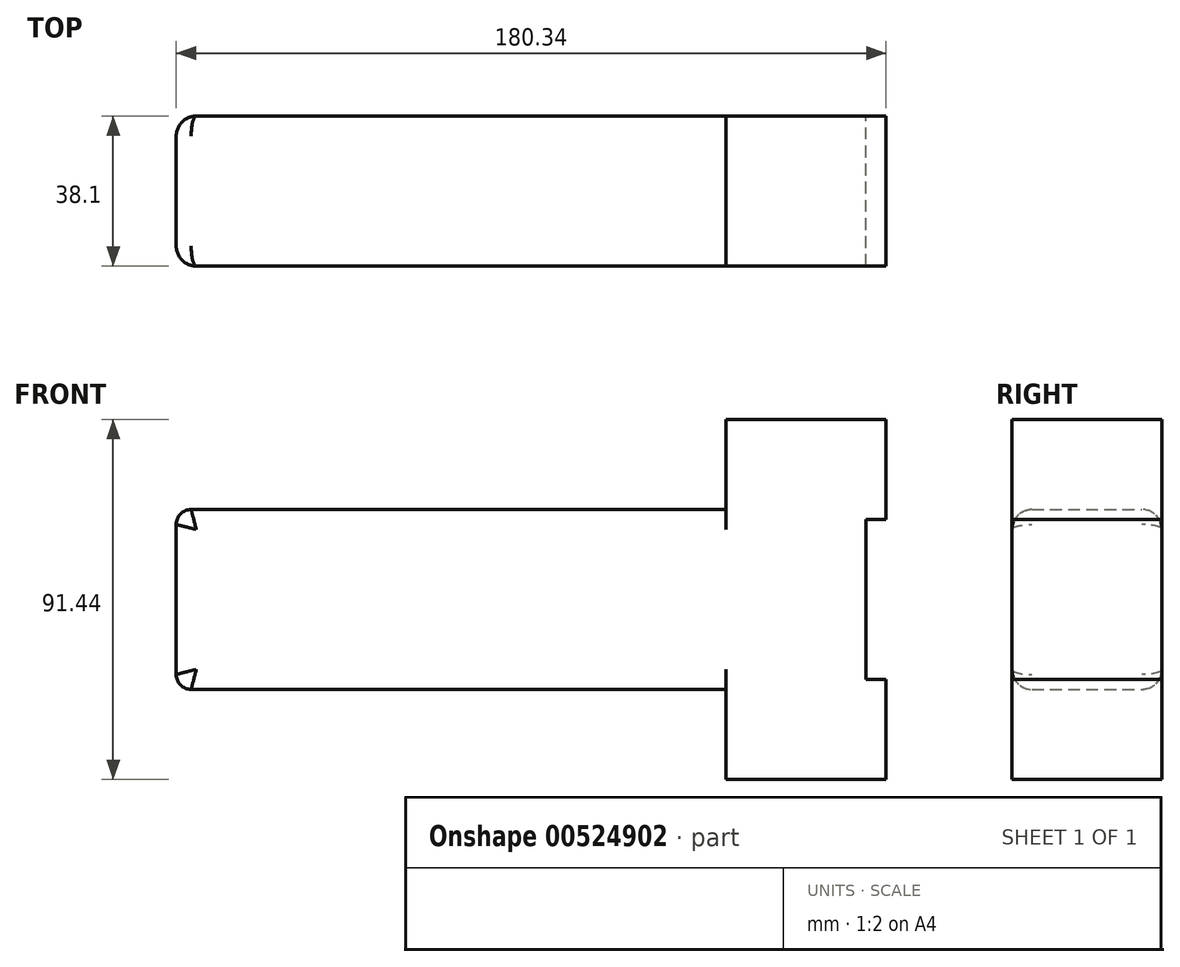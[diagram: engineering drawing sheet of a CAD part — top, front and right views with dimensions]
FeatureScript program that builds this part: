
annotation { "Feature Type Name" : "Feature", "Feature Type Description" : "" }
export const myFeature = defineFeature(function(context is Context, id is Id, definition is map)
    precondition{}
    {
        {
            var Q0;
            Q0=qCreatedBy(makeId("Front.planeOp"),FACE);
            var sketch = newSketch(context, id + "F0", { "sketchPlane" : qUnion([Q0])});
            skLineSegment(sketch, "E0.bottom", {"start": v(69.85, -22.86) * mm, "end": v(-66.04, -22.86) * mm});
            skLineSegment(sketch, "E0.top", {"start": v(69.85, 22.86) * mm, "end": v(-66.04, 22.86) * mm});
            skLineSegment(sketch, "E0.left", {"start": v(69.85, -22.86) * mm, "end": v(69.85, 22.86) * mm});
            skLineSegment(sketch, "E0.right", {"start": v(-69.85, -19.05) * mm, "end": v(-69.85, 19.05) * mm});
            skPoint(sketch, "E0.middle", {"position": v(0, 0) * mm});
            skLineSegment(sketch, "E1.bottom", {"start": v(110.5, -45.72) * mm, "end": v(69.85, -45.72) * mm});
            skLineSegment(sketch, "E1.top", {"start": v(110.5, 45.72) * mm, "end": v(69.85, 45.72) * mm});
            skLineSegment(sketch, "E1.left", {"start": v(110.5, -45.72) * mm, "end": v(110.5, -20.32) * mm});
            skLineSegment(sketch, "E1.right", {"start": v(69.85, -45.72) * mm, "end": v(69.85, 45.72) * mm});
            skPoint(sketch, "E1.middle", {"position": v(90.17, 0) * mm});
            skPoint(sketch, "E2.visualSharp", {"position": v(-69.85, 22.86) * mm});
            skArc(sketch, "E2.filletArc", {"start": v(-66.04, 22.86) * mm, "mid": v(-68.73, 21.74) * mm, "end": v(-69.85, 19.05) * mm});
            skPoint(sketch, "E3.visualSharp", {"position": v(-69.85, -22.86) * mm});
            skArc(sketch, "E3.filletArc", {"start": v(-69.85, -19.05) * mm, "mid": v(-68.73, -21.74) * mm, "end": v(-66.04, -22.86) * mm});
            skLineSegment(sketch, "E4", {"start": v(-69.85, -19.05) * mm, "end": v(31.75, -19.05) * mm});
            skLineSegment(sketch, "E5", {"start": v(-69.85, 19.05) * mm, "end": v(31.75, 19.05) * mm});
            skLineSegment(sketch, "E6", {"start": v(31.75, -22.86) * mm, "end": v(31.75, 22.86) * mm});
            skPoint(sketch, "E7", {"position": v(47, -22.86) * mm});
            skArc(sketch, "E8", {"start": v(31.75, -19.05) * mm, "mid": v(39.6, -20.02) * mm, "end": v(47, -22.86) * mm});
            skPoint(sketch, "E9", {"position": v(47, 22.86) * mm});
            skArc(sketch, "E10", {"start": v(31.75, 19.05) * mm, "mid": v(39.6, 20.02) * mm, "end": v(46.99, 22.86) * mm});
            skLineSegment(sketch, "E11.bottom", {"start": v(110.5, 20.32) * mm, "end": v(105.41, 20.32) * mm});
            skLineSegment(sketch, "E11.top", {"start": v(110.5, -20.32) * mm, "end": v(105.41, -20.32) * mm});
            skLineSegment(sketch, "E11.right", {"start": v(105.41, 20.32) * mm, "end": v(105.41, -20.32) * mm});
            skPoint(sketch, "E11.middle", {"position": v(110.5, 0) * mm});
            skLineSegment(sketch, "E12.trimOffspring", {"start": v(110.5, 20.32) * mm, "end": v(110.5, 45.72) * mm});
            skSolve(sketch);
        }
        {
            var Q0;
            {var subQ5=sQuery(id+"F0.wireOp",EDGE,"E8");Q0=makeQuery(id+"F0.imprint","IMPRINT",FACE,{"disambiguationData":[TD([[makeQuery(id+"F0.imprint","IMPRINT",EDGE,{"derivedFrom":subQ5}),1.0]])]});}
            var Q1;
            Q1=makeQuery(id+"F0.imprint","IMPRINT",FACE,{"disambiguationData":[TD([[makeQuery(id+"F0.imprint","IMPRINT",EDGE,{"derivedFrom":sQuery(id+"F0.wireOp",EDGE,"E0.right")}),-1.0]])]});
            var Q2;
            {var subQ0=sQuery(id+"F0.wireOp",EDGE,"E2.filletArc");Q2=makeQuery(id+"F0.imprint","IMPRINT",FACE,{"disambiguationData":[TD([[makeQuery(id+"F0.imprint","IMPRINT",EDGE,{"derivedFrom":subQ0}),1.0]])]});}
            var Q3;
            {var subQ3=sQuery(id+"F0.wireOp",EDGE,"E10");Q3=makeQuery(id+"F0.imprint","IMPRINT",FACE,{"disambiguationData":[TD([[makeQuery(id+"F0.imprint","IMPRINT",EDGE,{"derivedFrom":subQ3}),1.0]])]});}
            var Q4;
            {var subQ0=sQuery(id+"F0.wireOp",EDGE,"E3.filletArc");Q4=makeQuery(id+"F0.imprint","IMPRINT",FACE,{"disambiguationData":[TD([[makeQuery(id+"F0.imprint","IMPRINT",EDGE,{"derivedFrom":subQ0}),1.0]])]});}
            var Q5;
            {var subQ3=sQuery(id+"F0.wireOp",EDGE,"E8");Q5=makeQuery(id+"F0.imprint","IMPRINT",FACE,{"disambiguationData":[TD([[makeQuery(id+"F0.imprint","IMPRINT",EDGE,{"derivedFrom":subQ3}),-1.0]])]});}
            var Q6;
            {var subQ2=sQuery(id+"F0.wireOp",EDGE,"E1.bottom");Q6=makeQuery(id+"F0.imprint","IMPRINT",FACE,{"disambiguationData":[TD([[makeQuery(id+"F0.imprint","IMPRINT",EDGE,{"derivedFrom":subQ2}),-1.0]])]});}
            extrude(context, id + "F1", {"entities" : qUnion([Q0, Q1, Q2, Q3, Q4, Q5, Q6]), "depth" : 38.1 * mm, "offsetDistance" : 25.4 * mm});
        }
        {
            var Q0;
            Q0=makeQuery(id+"F1.opExtrude","CAP_EDGE",EDGE,{"disambiguationData":[OSD([sQuery(id+"F0.wireOp",EDGE,"E0.top")])],"isStart":false});
            var Q1;
            Q1=makeQuery(id+"F1.opExtrude","CAP_EDGE",EDGE,{"disambiguationData":[OSD([sQuery(id+"F0.wireOp",EDGE,"E0.top")])],"isStart":true});
            var Q2;
            Q2=makeQuery(id+"F1.opExtrude","CAP_EDGE",EDGE,{"disambiguationData":[OSD([sQuery(id+"F0.wireOp",EDGE,"E0.bottom")])],"isStart":false});
            var Q3;
            Q3=makeQuery(id+"F1.opExtrude","CAP_EDGE",EDGE,{"disambiguationData":[OSD([sQuery(id+"F0.wireOp",EDGE,"E0.bottom")])],"isStart":true});
            fillet(context, id + "F2", {"entities" : qUnion([Q0, Q1, Q2, Q3]), "radius" : 5.08 * mm, "tangentPropagation" : true, "allowEdgeOverflow" : false});
        }
    });
